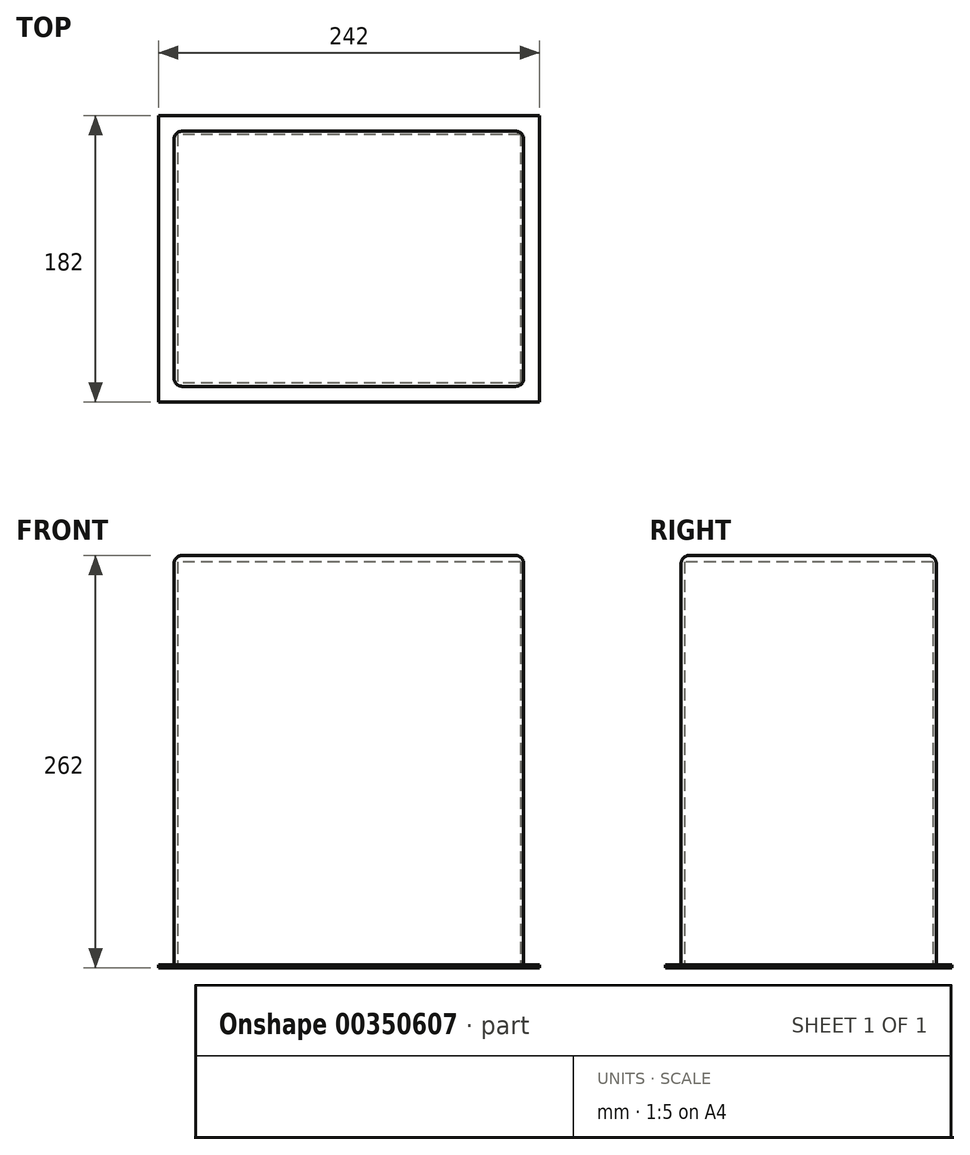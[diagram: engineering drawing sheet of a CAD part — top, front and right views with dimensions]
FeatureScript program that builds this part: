
annotation { "Feature Type Name" : "Feature", "Feature Type Description" : "" }
export const myFeature = defineFeature(function(context is Context, id is Id, definition is map)
    precondition{}
    {
        {
            var Q0;
            Q0=qCreatedBy(makeId("Top.planeOp"),FACE);
            var sketch = newSketch(context, id + "F0", { "sketchPlane" : qUnion([Q0])});
            skLineSegment(sketch, "E0.bottom", {"start": v(-111, -81) * mm, "end": v(111, -81) * mm});
            skLineSegment(sketch, "E0.top", {"start": v(-111, 81) * mm, "end": v(111, 81) * mm});
            skLineSegment(sketch, "E0.left", {"start": v(-111, -81) * mm, "end": v(-111, 81) * mm});
            skLineSegment(sketch, "E0.right", {"start": v(111, -81) * mm, "end": v(111, 81) * mm});
            skPoint(sketch, "E0.middle", {"position": v(0, 0) * mm});
            skSolve(sketch);
        }
        {
            var Q0;
            Q0=makeQuery(id+"F0.imprint","IMPRINT",FACE,{"disambiguationData":[TD([[makeQuery(id+"F0.imprint","IMPRINT",EDGE,{"derivedFrom":sQuery(id+"F0.wireOp",EDGE,"E0.bottom")}),1.0]])]});
            extrude(context, id + "F1", {"entities" : qUnion([Q0]), "depth" : 260 * mm});
        }
        {
            var Q0;
            Q0=makeQuery(id+"F1.opExtrude","CAP_FACE",FACE,{"disambiguationData":[OSD([sQuery(id+"F0.wireOp",EDGE,"E0.bottom"),sQuery(id+"F0.wireOp",EDGE,"E0.top"),sQuery(id+"F0.wireOp",EDGE,"E0.left"),sQuery(id+"F0.wireOp",EDGE,"E0.right")])],"isStart":true});
            var sketch = newSketch(context, id + "F2", { "sketchPlane" : qUnion([Q0])});
            skLineSegment(sketch, "E1.bottom", {"start": v(121, -91) * mm, "end": v(-121, -91) * mm});
            skLineSegment(sketch, "E1.top", {"start": v(121, 91) * mm, "end": v(-121, 91) * mm});
            skLineSegment(sketch, "E1.left", {"start": v(121, -91) * mm, "end": v(121, 91) * mm});
            skLineSegment(sketch, "E1.right", {"start": v(-121, -91) * mm, "end": v(-121, 91) * mm});
            skPoint(sketch, "E1.middle", {"position": v(0, 0) * mm});
            skSolve(sketch);
        }
        {
            var Q0;
            Q0 = qSketchRegion(id + "F2", true);
            extrude(context, id + "F3", {"entities" : qUnion([Q0]), "operationType" : NewBodyOperationType.ADD, "depth" : 2 * mm});
        }
        {
            var Q0;
            Q0=makeQuery(id+"F1.opExtrude","CAP_EDGE",EDGE,{"disambiguationData":[OSD([sQuery(id+"F0.wireOp",EDGE,"E0.bottom")])],"isStart":false});
            var Q1;
            Q1=makeQuery(id+"F1.opExtrude","CAP_EDGE",EDGE,{"disambiguationData":[OSD([sQuery(id+"F0.wireOp",EDGE,"E0.right")])],"isStart":false});
            var Q2;
            Q2=makeQuery(id+"F1.opExtrude","CAP_EDGE",EDGE,{"disambiguationData":[OSD([sQuery(id+"F0.wireOp",EDGE,"E0.top")])],"isStart":false});
            var Q3;
            Q3=makeQuery(id+"F1.opExtrude","CAP_EDGE",EDGE,{"disambiguationData":[OSD([sQuery(id+"F0.wireOp",EDGE,"E0.left")])],"isStart":false});
            var Q4;
            Q4=makeQuery(id+"F1.opExtrude","SWEPT_EDGE",EDGE,{"disambiguationData":[OSD([sQuery(id+"F0.wireOp",EDGE,"E0.bottom"),sQuery(id+"F0.wireOp",EDGE,"E0.right")])]});
            var Q5;
            Q5=makeQuery(id+"F1.opExtrude","SWEPT_EDGE",EDGE,{"disambiguationData":[OSD([sQuery(id+"F0.wireOp",EDGE,"E0.bottom"),sQuery(id+"F0.wireOp",EDGE,"E0.left")])]});
            var Q6;
            Q6=makeQuery(id+"F1.opExtrude","SWEPT_EDGE",EDGE,{"disambiguationData":[OSD([sQuery(id+"F0.wireOp",EDGE,"E0.top"),sQuery(id+"F0.wireOp",EDGE,"E0.right")])]});
            var Q7;
            Q7=makeQuery(id+"F1.opExtrude","SWEPT_EDGE",EDGE,{"disambiguationData":[OSD([sQuery(id+"F0.wireOp",EDGE,"E0.top"),sQuery(id+"F0.wireOp",EDGE,"E0.left")])]});
            fillet(context, id + "F4", {"entities" : qUnion([Q0, Q1, Q2, Q3, Q4, Q5, Q6, Q7]), "radius" : 5 * mm, "tangentPropagation" : true, "allowEdgeOverflow" : false});
        }
        {
            var Q0;
            Q0=qCreatedBy(makeId("Right.planeOp"),FACE);
            var sketch = newSketch(context, id + "F5", { "sketchPlane" : qUnion([Q0])});
            skLineSegment(sketch, "E2", {"start": v(-81, 20.15) * mm, "end": v(-101, 20.15) * mm});
            skLineSegment(sketch, "E3", {"start": v(-101, 40.15) * mm, "end": v(-81, 40.15) * mm});
            skLineSegment(sketch, "E4", {"start": v(-81, 40.15) * mm, "end": v(-81, 20.15) * mm});
            skArc(sketch, "E5", {"start": v(-101, 40.15) * mm, "mid": v(-111, 30.15) * mm, "end": v(-101, 20.15) * mm});
            skCircle(sketch, "E6", {"center": v(-101, 30.15) * mm, "radius": 4 * mm});
            skSolve(sketch);
        }
        {
            var Q0;
            Q0=makeQuery(id+"F5.imprint","IMPRINT",FACE,{"disambiguationData":[TD([[makeQuery(id+"F5.imprint","IMPRINT",EDGE,{"derivedFrom":sQuery(id+"F5.wireOp",EDGE,"E2")}),-1.0]])]});
            extrude(context, id + "F6", {"entities" : qUnion([Q0]), "depth" : 2 * mm});
        }
        {
            var Q0;
            Q0=makeQuery(id+"F3.opExtrude","CAP_FACE",FACE,{"disambiguationData":[OSD([sQuery(id+"F2.wireOp",EDGE,"E1.bottom"),sQuery(id+"F2.wireOp",EDGE,"E1.top"),sQuery(id+"F2.wireOp",EDGE,"E1.left"),sQuery(id+"F2.wireOp",EDGE,"E1.right")])],"isStart":false});
            var sketch = newSketch(context, id + "F7", { "sketchPlane" : qUnion([Q0])});
            skLineSegment(sketch, "E7.bottom", {"start": v(109, -79) * mm, "end": v(-109, -79) * mm});
            skLineSegment(sketch, "E7.top", {"start": v(109, 79) * mm, "end": v(-109, 79) * mm});
            skLineSegment(sketch, "E7.left", {"start": v(109, -79) * mm, "end": v(109, 79) * mm});
            skLineSegment(sketch, "E7.right", {"start": v(-109, -79) * mm, "end": v(-109, 79) * mm});
            skPoint(sketch, "E7.middle", {"position": v(0, 0) * mm});
            skSolve(sketch);
        }
        {
            var Q0;
            Q0 = qSketchRegion(id + "F7", true);
            extrude(context, id + "F8", {"entities" : qUnion([Q0]), "operationType" : NewBodyOperationType.REMOVE, "oppositeDirection" : true, "depth" : 258 * mm});
        }
        {
            var Q0;
            Q0=makeQuery(id+"F6.opExtrude","SWEPT_BODY",BODY,{"disambiguationData":[OSD([sQuery(id+"F5.wireOp",EDGE,"E2"),sQuery(id+"F5.wireOp",EDGE,"E3"),sQuery(id+"F5.wireOp",EDGE,"E4"),sQuery(id+"F5.wireOp",EDGE,"E5"),sQuery(id+"F5.wireOp",EDGE,"E6")])]});
            deleteBodies(context, id + "F9", {"entities" : qUnion([Q0])});
        }
    });
